# Revit family: QF_Varimixer_AR60
name_source: partatom
category: Specialty Equipment
units: mm (PartAtom-declared; Revit-internal decimal feet)

## family parameters
Always vertical = Yes
Cut with Voids When Loaded = No
OmniClass Number = 23.40.40.14.14.11
OmniClass Title = Food Mixers
Part Type = Normal
Room Calculation Point = No
Round Connector Dimension = Use Diameter
Shared = No
Work Plane-Based = No

## types (7) — shared parameters
Bowl size = 60 liter
Depth = 1028.7 mm
Description = Planetary mixer AR60
Electrical connection height = 1175 mm
Height = 1412.875 mm
Homepage = https://www.varimixer.com
Ingress Protection = IP32
Length = 647.7 mm
Manufacturer = VARIMIXER A/S
Model = AR60
Panel name = VL-1 (manual) or VL-1S (electrical)
Product description = Planetary mixer, heavy duty for whiping, kneading and mixing
Product name = AR60
URL = www.varimixer.com
URL Datasheet = https://www.varimixer.com
Weight in Pounds = 456
Weight in kilograms = 275

## per-type parameters (varying)
| type | Connected with neutral | Cycle | Full load current | Horsepower | Number of phases | Plug included | Power | Voltage |
| 200V/50Hz/3Ph/Japan | Yes | 50 Hz | 9 A |  | 3 | No | 1900 W | 200 V |
| 208V/60Hz/1Ph/USA | Yes | 60 Hz | 11 A | 3 hp | 1 | Yes | 1900 W | 208 V |
| 200V/60Hz/3Ph/Japan | Yes | 60 Hz | 6 A |  | 3 | Yes | 1900 W | 200 V |
| 208V/60Hz/3Ph/USA | Yes | 60 Hz | 6 A | 3 hp | 3 | Yes | 2200 W | 208 V |
| 230V/50Hz/1Ph/Europe | Yes | 50 Hz | 12 A |  | 1 | Yes | 1500 W | 230 V |
| 400V/50Hz/3Ph/Europe | Yes | 50 Hz | 5 A |  | 3 | No | 1900 W | 400 V |
| Others on request | No | 0 Hz | 0 A |  | 0 | No | 0 W | 0 V |

## geometry (parser evidence)
native form markers: Blend x2, Sweep x5
no freeform markers — native parametric forms only
